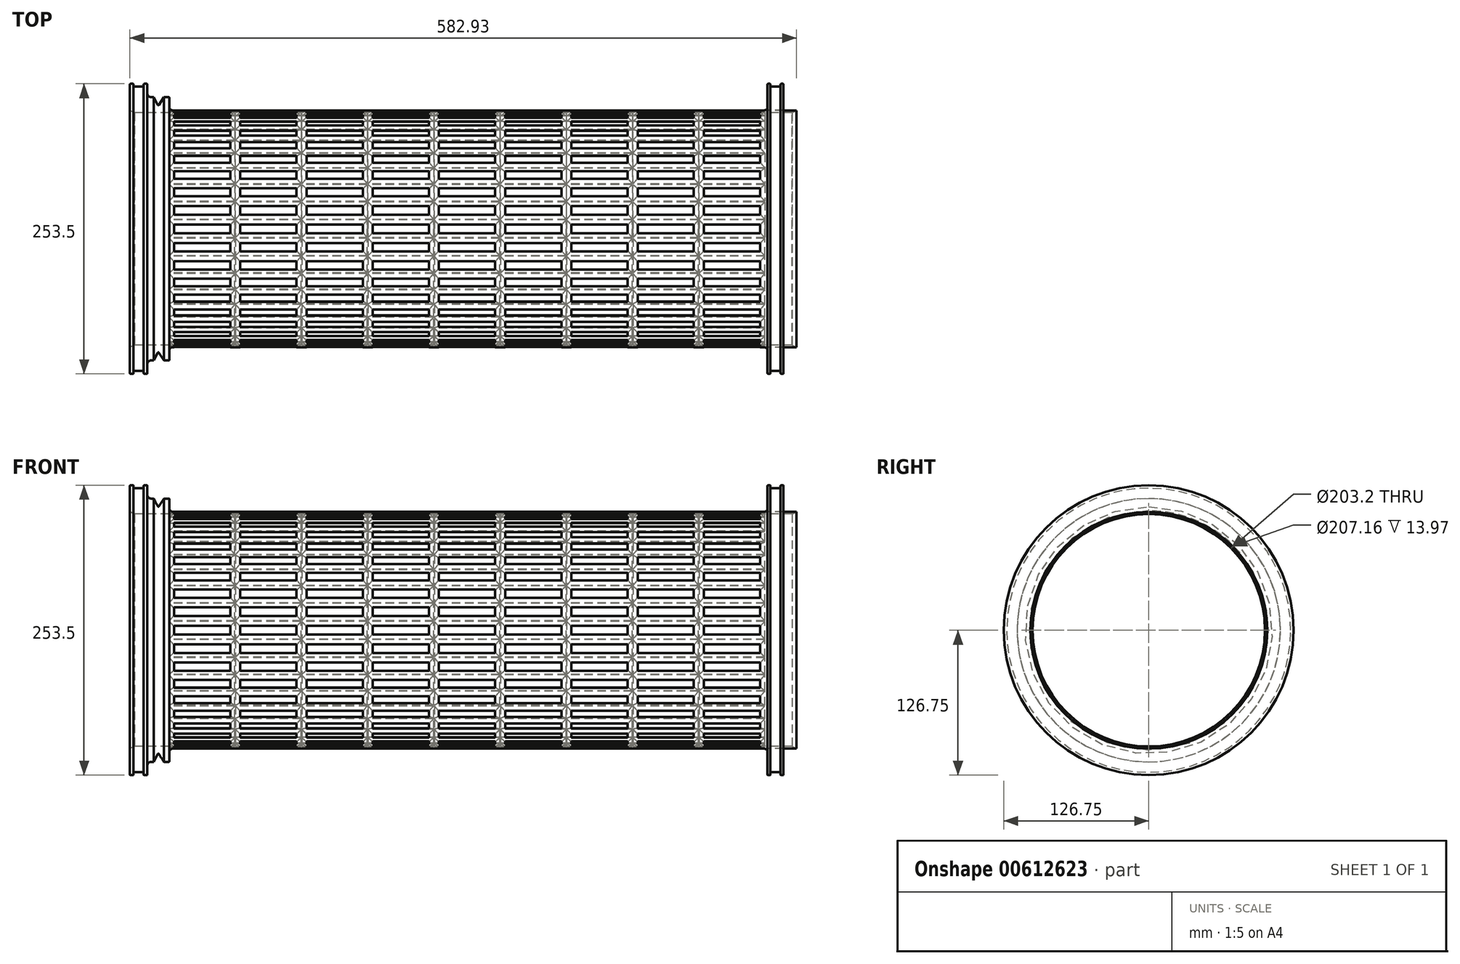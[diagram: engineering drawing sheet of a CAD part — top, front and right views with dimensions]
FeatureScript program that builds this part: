
annotation { "Feature Type Name" : "Feature", "Feature Type Description" : "" }
export const myFeature = defineFeature(function(context is Context, id is Id, definition is map)
    precondition{}
    {
        {
            var Q0;
            Q0=qCreatedBy(makeId("Top.planeOp"),FACE);
            var sketch = newSketch(context, id + "F0", { "sketchPlane" : qUnion([Q0])});
            skLineSegment(sketch, "E0", {"start": v(-334.6, 103.5) * mm, "end": v(-334.6, 126.75) * mm});
            skLineSegment(sketch, "E1", {"start": v(-334.6, 126.75) * mm, "end": v(-331.43, 126.75) * mm});
            skLineSegment(sketch, "E2", {"start": v(-319.37, 126.75) * mm, "end": v(-319.37, 103.5) * mm});
            skLineSegment(sketch, "E3", {"start": v(-319.37, 103.5) * mm, "end": v(219.75, 103.5) * mm});
            skLineSegment(sketch, "E4", {"start": v(222.92, 106.68) * mm, "end": v(222.92, 126.75) * mm});
            skLineSegment(sketch, "E5", {"start": v(236.9, 126.75) * mm, "end": v(236.9, 103.58) * mm});
            skLineSegment(sketch, "E6", {"start": v(236.9, 103.5) * mm, "end": v(248.32, 103.5) * mm});
            skLineSegment(sketch, "E7", {"start": v(-334.6, 101.6) * mm, "end": v(248.32, 101.6) * mm});
            skLineSegment(sketch, "E8", {"start": v(248.32, 101.6) * mm, "end": v(248.32, 103.5) * mm});
            skLineSegment(sketch, "E9", {"start": v(-331.43, 126.75) * mm, "end": v(-331.43, 124.2) * mm});
            skLineSegment(sketch, "E10", {"start": v(-322.54, 124.2) * mm, "end": v(-322.54, 126.75) * mm});
            skLineSegment(sketch, "E11.trimOffspring", {"start": v(-322.54, 126.75) * mm, "end": v(-319.37, 126.75) * mm});
            skLineSegment(sketch, "E12", {"start": v(225.46, 126.75) * mm, "end": v(225.46, 124.2) * mm});
            skLineSegment(sketch, "E13", {"start": v(-300.16, 103.5) * mm, "end": v(-300.16, 115.13) * mm});
            skPoint(sketch, "E13.endSnap0", {"position": v(-319.37, 115.13) * mm});
            skLineSegment(sketch, "E14", {"start": v(-300.16, 115.13) * mm, "end": v(-304.87, 115.13) * mm});
            skLineSegment(sketch, "E15", {"start": v(-313.74, 115.13) * mm, "end": v(-309.76, 107.51) * mm});
            skPoint(sketch, "E15.endSnap0", {"position": v(-309.76, 115.13) * mm});
            skLineSegment(sketch, "E16", {"start": v(-309.76, 107.51) * mm, "end": v(-304.87, 115.13) * mm});
            skLineSegment(sketch, "E17.trimOffspring", {"start": v(-313.74, 115.13) * mm, "end": v(-319.37, 115.13) * mm});
            skLineSegment(sketch, "E18", {"start": v(-334.6, 103.5) * mm, "end": v(-334.6, 101.6) * mm});
            skPoint(sketch, "E19.end.orphan", {"position": v(-353.66, 101.6) * mm});
            skLineSegment(sketch, "E20", {"start": v(222.92, 126.75) * mm, "end": v(225.46, 126.75) * mm});
            skPoint(sketch, "E20.startSnap0", {"position": v(225.46, 126.75) * mm});
            skPoint(sketch, "E21.start.orphan", {"position": v(222.92, 126.75) * mm});
            skPoint(sketch, "E22.orphan", {"position": v(225.46, 129.3) * mm});
            skPoint(sketch, "E23.trimOffspring.start.orphan", {"position": v(233.08, 126.75) * mm});
            skPoint(sketch, "E24.end.orphan", {"position": v(233.08, 124.2) * mm});
            skLineSegment(sketch, "E25", {"start": v(225.46, 124.2) * mm, "end": v(234.35, 124.2) * mm});
            skLineSegment(sketch, "E26", {"start": v(234.35, 124.2) * mm, "end": v(234.35, 126.11) * mm});
            skPoint(sketch, "E26.endSnap0", {"position": v(234.99, 126.11) * mm});
            skPoint(sketch, "E27.orphan", {"position": v(233.08, 125.48) * mm});
            skLineSegment(sketch, "E28", {"start": v(-331.43, 124.2) * mm, "end": v(-322.54, 124.2) * mm});
            skLineSegment(sketch, "E29", {"start": v(234.35, 126.11) * mm, "end": v(234.35, 126.75) * mm});
            skLineSegment(sketch, "E30", {"start": v(234.35, 126.75) * mm, "end": v(236.9, 126.75) * mm});
            skPoint(sketch, "E31.visualSharp", {"position": v(222.92, 103.5) * mm});
            skArc(sketch, "E31.filletArc", {"start": v(219.75, 103.5) * mm, "mid": v(222, 104.43) * mm, "end": v(222.92, 106.68) * mm});
            skLineSegment(sketch, "E32", {"start": v(236.9, 103.5) * mm, "end": v(222.92, 103.5) * mm});
            skLineSegment(sketch, "E33", {"start": v(222.92, 103.5) * mm, "end": v(222.92, 106.68) * mm});
            skLineSegment(sketch, "E34", {"start": v(236.9, 103.58) * mm, "end": v(222.92, 103.58) * mm});
            skSolve(sketch);
        }
        {
            var Q0;
            Q0=qCreatedBy(makeId("Top.planeOp"),FACE);
            var sketch = newSketch(context, id + "F1", { "sketchPlane" : qUnion([Q0])});
            skLineSegment(sketch, "E35", {"start": v(-76.35, 0) * mm, "end": v(75.96, 0) * mm});
            skSolve(sketch);
        }
        {
            var Q0;
            Q0=makeQuery(id+"F0.imprint","IMPRINT",FACE,{"disambiguationData":[TD([[makeQuery(id+"F0.imprint","IMPRINT",EDGE,{"derivedFrom":sQuery(id+"F0.wireOp",EDGE,"E0")}),-1.0]])]});
            var Q1;
            {var subQ0=sQuery(id+"F0.wireOp",EDGE,"E13");Q1=makeQuery(id+"F0.imprint","IMPRINT",FACE,{"disambiguationData":[TD([[makeQuery(id+"F0.imprint","IMPRINT",EDGE,{"derivedFrom":subQ0}),1.0]])]});}
            var Q2;
            Q2=qSketchRegion(id+"F3",true);
            var Q3;
            Q3=sQuery(id+"F1.wireOp",EDGE,"E35");
            revolve(context, id + "F2", {"entities" : qUnion([Q0, Q1, Q2]), "axis" : qUnion([Q3]), "revolveType" : RevolveType.FULL, "surfaceOperationType" : NewSurfaceOperationType.NEW});
        }
        {
            var Q0;
            Q0=qCreatedBy(makeId("Top.planeOp"),FACE);
            var sketch = newSketch(context, id + "F3", { "sketchPlane" : qUnion([Q0])});
            skPoint(sketch, "E36.middle", {"position": v(-205.28, 0) * mm});
            skPoint(sketch, "E37.middle", {"position": v(0, 0) * mm});
            skPoint(sketch, "E38.middle", {"position": v(166.22, 0) * mm});
            skLineSegment(sketch, "E39", {"start": v(-296.04, -3.81) * mm, "end": v(-296.04, 3.81) * mm});
            skPoint(sketch, "E40.orphan", {"position": v(-306.88, -3.81) * mm});
            skPoint(sketch, "E41.orphan", {"position": v(-306.88, 3.81) * mm});
            skPoint(sketch, "E38.left.start.orphan", {"position": v(229.72, -3.81) * mm});
            skPoint(sketch, "E42.orphan", {"position": v(229.72, 3.8) * mm});
            skLineSegment(sketch, "E43", {"start": v(-246.86, 3.81) * mm, "end": v(-246.86, -3.81) * mm});
            skLineSegment(sketch, "E44.trimOffspring", {"start": v(-246.86, 3.81) * mm, "end": v(-296.04, 3.81) * mm});
            skLineSegment(sketch, "E45.trimOffspring", {"start": v(-246.86, -3.81) * mm, "end": v(-296.04, -3.81) * mm});
            skPoint(sketch, "E46.end.orphan", {"position": v(-171.63, 3.81) * mm});
            skPoint(sketch, "E46.start.orphan", {"position": v(-171.63, -3.81) * mm});
            skPoint(sketch, "E47.end.orphan", {"position": v(-239.58, -3.81) * mm});
            skPoint(sketch, "E47.start.orphan", {"position": v(-239.58, 3.81) * mm});
            skPoint(sketch, "E36.left.end.orphan", {"position": v(-103.68, 3.81) * mm});
            skPoint(sketch, "E36.left.start.orphan", {"position": v(-103.68, -3.8) * mm});
            skPoint(sketch, "E37.bottom.end.orphan", {"position": v(-93.22, 3.98) * mm});
            skPoint(sketch, "E37.top.end.orphan", {"position": v(-93.22, -3.98) * mm});
            skPoint(sketch, "E37.left.end.orphan", {"position": v(93.22, -3.98) * mm});
            skPoint(sketch, "E37.left.start.orphan", {"position": v(93.22, 3.98) * mm});
            skPoint(sketch, "E38.bottom.end.orphan", {"position": v(102.72, -3.81) * mm});
            skPoint(sketch, "E38.top.end.orphan", {"position": v(102.72, 3.8) * mm});
            skLineSegment(sketch, "E48.1.0.0", {"start": v(-238.12, -3.81) * mm, "end": v(-238.12, 3.81) * mm});
            skLineSegment(sketch, "E48.1.0.1", {"start": v(-188.95, -3.81) * mm, "end": v(-238.12, -3.81) * mm});
            skLineSegment(sketch, "E48.1.0.2", {"start": v(-188.95, 3.81) * mm, "end": v(-188.95, -3.81) * mm});
            skLineSegment(sketch, "E48.1.0.3", {"start": v(-188.95, 3.81) * mm, "end": v(-238.12, 3.81) * mm});
            skLineSegment(sketch, "E48.2.0.0", {"start": v(-180.21, -3.81) * mm, "end": v(-180.21, 3.81) * mm});
            skLineSegment(sketch, "E48.2.0.1", {"start": v(-131.04, -3.81) * mm, "end": v(-180.21, -3.81) * mm});
            skLineSegment(sketch, "E48.2.0.2", {"start": v(-131.04, 3.81) * mm, "end": v(-131.04, -3.81) * mm});
            skLineSegment(sketch, "E48.2.0.3", {"start": v(-131.04, 3.81) * mm, "end": v(-180.21, 3.81) * mm});
            skLineSegment(sketch, "E48.3.0.0", {"start": v(-122.3, -3.81) * mm, "end": v(-122.3, 3.81) * mm});
            skLineSegment(sketch, "E48.3.0.1", {"start": v(-73.13, -3.81) * mm, "end": v(-122.3, -3.81) * mm});
            skLineSegment(sketch, "E48.3.0.2", {"start": v(-73.13, 3.81) * mm, "end": v(-73.13, -3.81) * mm});
            skLineSegment(sketch, "E48.3.0.3", {"start": v(-73.13, 3.81) * mm, "end": v(-122.3, 3.81) * mm});
            skLineSegment(sketch, "E48.4.0.0", {"start": v(-64.39, -3.81) * mm, "end": v(-64.39, 3.81) * mm});
            skLineSegment(sketch, "E48.4.0.1", {"start": v(-15.22, -3.81) * mm, "end": v(-64.39, -3.81) * mm});
            skLineSegment(sketch, "E48.4.0.2", {"start": v(-15.22, 3.81) * mm, "end": v(-15.22, -3.81) * mm});
            skLineSegment(sketch, "E48.4.0.3", {"start": v(-15.22, 3.81) * mm, "end": v(-64.39, 3.81) * mm});
            skLineSegment(sketch, "E48.5.0.0", {"start": v(-6.48, -3.81) * mm, "end": v(-6.48, 3.81) * mm});
            skLineSegment(sketch, "E48.5.0.1", {"start": v(42.7, -3.81) * mm, "end": v(-6.48, -3.81) * mm});
            skLineSegment(sketch, "E48.5.0.2", {"start": v(42.7, 3.81) * mm, "end": v(42.7, -3.81) * mm});
            skLineSegment(sketch, "E48.5.0.3", {"start": v(42.7, 3.81) * mm, "end": v(-6.48, 3.81) * mm});
            skLineSegment(sketch, "E48.6.0.0", {"start": v(51.44, -3.81) * mm, "end": v(51.44, 3.81) * mm});
            skLineSegment(sketch, "E48.6.0.1", {"start": v(100.6, -3.81) * mm, "end": v(51.44, -3.81) * mm});
            skLineSegment(sketch, "E48.6.0.2", {"start": v(100.6, 3.81) * mm, "end": v(100.6, -3.81) * mm});
            skLineSegment(sketch, "E48.6.0.3", {"start": v(100.6, 3.81) * mm, "end": v(51.44, 3.81) * mm});
            skLineSegment(sketch, "E48.7.0.0", {"start": v(109.35, -3.81) * mm, "end": v(109.35, 3.81) * mm});
            skLineSegment(sketch, "E48.7.0.1", {"start": v(158.52, -3.81) * mm, "end": v(109.35, -3.81) * mm});
            skLineSegment(sketch, "E48.7.0.2", {"start": v(158.52, 3.81) * mm, "end": v(158.52, -3.81) * mm});
            skLineSegment(sketch, "E48.7.0.3", {"start": v(158.52, 3.81) * mm, "end": v(109.35, 3.81) * mm});
            skLineSegment(sketch, "E48.8.0.0", {"start": v(167.26, -3.81) * mm, "end": v(167.26, 3.81) * mm});
            skLineSegment(sketch, "E48.8.0.1", {"start": v(216.43, -3.81) * mm, "end": v(167.26, -3.81) * mm});
            skLineSegment(sketch, "E48.8.0.2", {"start": v(216.43, 3.81) * mm, "end": v(216.43, -3.81) * mm});
            skLineSegment(sketch, "E48.8.0.3", {"start": v(216.43, 3.81) * mm, "end": v(167.26, 3.81) * mm});
            skLineSegment(sketch, "E48.direction1", {"start": v(-296.04, -3.81) * mm, "end": v(-238.12, -3.81) * mm, "construction": true});
            skSolve(sketch);
        }
        {
            var Q0;
            Q0=qSketchRegion(id+"F3",true);
            extrude(context, id + "F4", {"entities" : qUnion([Q0]), "depth" : 114.3 * mm, "offsetDistance" : 25.4 * mm});
        }
        {
            var Q0;
            Q0=makeQuery(id+"F4.opExtrude","SWEPT_BODY",BODY,{"disambiguationData":[OSD([sQuery(id+"F3.wireOp",EDGE,"E48.8.0.0"),sQuery(id+"F3.wireOp",EDGE,"E48.8.0.1"),sQuery(id+"F3.wireOp",EDGE,"E48.8.0.2"),sQuery(id+"F3.wireOp",EDGE,"E48.8.0.3")])]});
            var Q1;
            Q1=makeQuery(id+"F4.opExtrude","SWEPT_BODY",BODY,{"disambiguationData":[OSD([sQuery(id+"F3.wireOp",EDGE,"E48.7.0.0"),sQuery(id+"F3.wireOp",EDGE,"E48.7.0.1"),sQuery(id+"F3.wireOp",EDGE,"E48.7.0.2"),sQuery(id+"F3.wireOp",EDGE,"E48.7.0.3")])]});
            var Q2;
            Q2=makeQuery(id+"F4.opExtrude","SWEPT_BODY",BODY,{"disambiguationData":[OSD([sQuery(id+"F3.wireOp",EDGE,"E48.6.0.0"),sQuery(id+"F3.wireOp",EDGE,"E48.6.0.1"),sQuery(id+"F3.wireOp",EDGE,"E48.6.0.2"),sQuery(id+"F3.wireOp",EDGE,"E48.6.0.3")])]});
            var Q3;
            Q3=makeQuery(id+"F4.opExtrude","SWEPT_BODY",BODY,{"disambiguationData":[OSD([sQuery(id+"F3.wireOp",EDGE,"E48.5.0.0"),sQuery(id+"F3.wireOp",EDGE,"E48.5.0.1"),sQuery(id+"F3.wireOp",EDGE,"E48.5.0.2"),sQuery(id+"F3.wireOp",EDGE,"E48.5.0.3")])]});
            var Q4;
            Q4=makeQuery(id+"F4.opExtrude","SWEPT_BODY",BODY,{"disambiguationData":[OSD([sQuery(id+"F3.wireOp",EDGE,"E48.4.0.0"),sQuery(id+"F3.wireOp",EDGE,"E48.4.0.1"),sQuery(id+"F3.wireOp",EDGE,"E48.4.0.2"),sQuery(id+"F3.wireOp",EDGE,"E48.4.0.3")])]});
            var Q5;
            Q5=makeQuery(id+"F4.opExtrude","SWEPT_BODY",BODY,{"disambiguationData":[OSD([sQuery(id+"F3.wireOp",EDGE,"E48.3.0.0"),sQuery(id+"F3.wireOp",EDGE,"E48.3.0.1"),sQuery(id+"F3.wireOp",EDGE,"E48.3.0.2"),sQuery(id+"F3.wireOp",EDGE,"E48.3.0.3")])]});
            var Q6;
            Q6=makeQuery(id+"F4.opExtrude","SWEPT_BODY",BODY,{"disambiguationData":[OSD([sQuery(id+"F3.wireOp",EDGE,"E48.2.0.0"),sQuery(id+"F3.wireOp",EDGE,"E48.2.0.1"),sQuery(id+"F3.wireOp",EDGE,"E48.2.0.2"),sQuery(id+"F3.wireOp",EDGE,"E48.2.0.3")])]});
            var Q7;
            Q7=makeQuery(id+"F4.opExtrude","SWEPT_BODY",BODY,{"disambiguationData":[OSD([sQuery(id+"F3.wireOp",EDGE,"E48.1.0.0"),sQuery(id+"F3.wireOp",EDGE,"E48.1.0.1"),sQuery(id+"F3.wireOp",EDGE,"E48.1.0.2"),sQuery(id+"F3.wireOp",EDGE,"E48.1.0.3")])]});
            var Q8;
            Q8=makeQuery(id+"F4.opExtrude","SWEPT_BODY",BODY,{"disambiguationData":[OSD([sQuery(id+"F3.wireOp",EDGE,"E39"),sQuery(id+"F3.wireOp",EDGE,"E43"),sQuery(id+"F3.wireOp",EDGE,"E44.trimOffspring"),sQuery(id+"F3.wireOp",EDGE,"E45.trimOffspring")])]});
            var Q9;
            Q9=makeQuery(id+"F2.opRevolve","SWEPT_FACE",FACE,{"disambiguationData":[OSD([sQuery(id+"F0.wireOp",EDGE,"E7")])]});
            circularPattern(context, id + "F5", {"operationType" : NewBodyOperationType.REMOVE, "entities" : qUnion([Q0, Q1, Q2, Q3, Q4, Q5, Q6, Q7, Q8]), "axis" : qUnion([Q9]), "angle" : 360 * degree, "instanceCount" : 40, "equalSpace" : true});
        }
        {
            var Q0;
            Q0=makeQuery(id+"F2.opRevolve","SWEPT_FACE",FACE,{"disambiguationData":[OSD([sQuery(id+"F0.wireOp",EDGE,"E7")])]});
            chamfer(context, id + "F6", {"entities" : qUnion([Q0]), "chamferType" : ChamferType.TWO_OFFSETS, "width1" : 4.06 * mm, "oppositeDirection" : false, "width2" : 1.9 * mm});
        }
        {
            var Q0;
            Q0=makeQuery(id+"F2.opRevolve","SWEPT_EDGE",EDGE,{"disambiguationData":[OSD([sQuery(id+"F0.wireOp",EDGE,"E2"),sQuery(id+"F0.wireOp",EDGE,"E17.trimOffspring")])]});
            var Q1;
            Q1=makeQuery(id+"F2.opRevolve","SWEPT_EDGE",EDGE,{"disambiguationData":[OSD([sQuery(id+"F0.wireOp",EDGE,"E3"),sQuery(id+"F0.wireOp",EDGE,"E13")])]});
            var Q2;
            Q2=makeQuery(id+"F2.opRevolve","SWEPT_EDGE",EDGE,{"disambiguationData":[OSD([sQuery(id+"F0.wireOp",EDGE,"E3"),sQuery(id+"F0.wireOp",EDGE,"E4")])]});
            var Q3;
            Q3=makeQuery(id+"F2.opRevolve","SWEPT_EDGE",EDGE,{"disambiguationData":[OSD([sQuery(id+"F0.wireOp",EDGE,"E5"),sQuery(id+"F0.wireOp",EDGE,"E6")])]});
            fillet(context, id + "F7", {"entities" : qUnion([Q0, Q1, Q2, Q3]), "radius" : 3.17 * mm, "tangentPropagation" : true, "allowEdgeOverflow" : false});
        }
        {
            var Q0;
            Q0=makeQuery(id+"F2.opRevolve","SWEPT_EDGE",EDGE,{"disambiguationData":[OSD([sQuery(id+"F0.wireOp",EDGE,"E10"),sQuery(id+"F0.wireOp",EDGE,"E28")])]});
            var Q1;
            Q1=makeQuery(id+"F2.opRevolve","SWEPT_EDGE",EDGE,{"disambiguationData":[OSD([sQuery(id+"F0.wireOp",EDGE,"E15"),sQuery(id+"F0.wireOp",EDGE,"E16")])]});
            var Q2;
            Q2=makeQuery(id+"F2.opRevolve","SWEPT_EDGE",EDGE,{"disambiguationData":[OSD([sQuery(id+"F0.wireOp",EDGE,"E13"),sQuery(id+"F0.wireOp",EDGE,"E14")])]});
            var Q3;
            Q3=makeQuery(id+"F2.opRevolve","SWEPT_EDGE",EDGE,{"disambiguationData":[OSD([sQuery(id+"F0.wireOp",EDGE,"E25"),sQuery(id+"F0.wireOp",EDGE,"E26")])]});
            var Q4;
            Q4=makeQuery(id+"F2.opRevolve","SWEPT_EDGE",EDGE,{"disambiguationData":[OSD([sQuery(id+"F0.wireOp",EDGE,"E4"),sQuery(id+"F0.wireOp",EDGE,"E20")])]});
            var Q5;
            Q5=makeQuery(id+"F2.opRevolve","SWEPT_EDGE",EDGE,{"disambiguationData":[OSD([sQuery(id+"F0.wireOp",EDGE,"E29"),sQuery(id+"F0.wireOp",EDGE,"E30")])]});
            var Q6;
            Q6=makeQuery(id+"F2.opRevolve","SWEPT_EDGE",EDGE,{"disambiguationData":[OSD([sQuery(id+"F0.wireOp",EDGE,"E5"),sQuery(id+"F0.wireOp",EDGE,"E30")])]});
            var Q7;
            Q7=makeQuery(id+"F2.opRevolve","SWEPT_EDGE",EDGE,{"disambiguationData":[OSD([sQuery(id+"F0.wireOp",EDGE,"E12"),sQuery(id+"F0.wireOp",EDGE,"E20")])]});
            var Q8;
            Q8=makeQuery(id+"F2.opRevolve","SWEPT_EDGE",EDGE,{"disambiguationData":[OSD([sQuery(id+"F0.wireOp",EDGE,"E10"),sQuery(id+"F0.wireOp",EDGE,"E11.trimOffspring")])]});
            var Q9;
            Q9=makeQuery(id+"F2.opRevolve","SWEPT_EDGE",EDGE,{"disambiguationData":[OSD([sQuery(id+"F0.wireOp",EDGE,"E0"),sQuery(id+"F0.wireOp",EDGE,"E1")])]});
            var Q10;
            Q10=makeQuery(id+"F2.opRevolve","SWEPT_EDGE",EDGE,{"disambiguationData":[OSD([sQuery(id+"F0.wireOp",EDGE,"E1"),sQuery(id+"F0.wireOp",EDGE,"E9")])]});
            var Q11;
            Q11=makeQuery(id+"F2.opRevolve","SWEPT_EDGE",EDGE,{"disambiguationData":[OSD([sQuery(id+"F0.wireOp",EDGE,"E2"),sQuery(id+"F0.wireOp",EDGE,"E11.trimOffspring")])]});
            fillet(context, id + "F8", {"entities" : qUnion([Q0, Q1, Q2, Q3, Q4, Q5, Q6, Q7, Q8, Q9, Q10, Q11]), "radius" : 0.5 * mm, "tangentPropagation" : true, "allowEdgeOverflow" : false});
        }
        {
            var Q0;
            Q0=makeQuery(id+"F0.imprint","IMPRINT",FACE,{"disambiguationData":[TD([[makeQuery(id+"F0.imprint","IMPRINT",EDGE,{"derivedFrom":sQuery(id+"F0.wireOp",EDGE,"E4")}),-1.0]])]});
            var Q1;
            Q1=sQuery(id+"F1.wireOp",EDGE,"E35");
            revolve(context, id + "F9", {"surfaceOperationType" : NewSurfaceOperationType.NEW, "entities" : qUnion([Q0]), "axis" : qUnion([Q1]), "revolveType" : RevolveType.FULL});
        }
        {
            var Q0;
            Q0=makeQuery(id+"F9.opRevolve","SWEPT_EDGE",EDGE,{"disambiguationData":[OSD([sQuery(id+"F0.wireOp",EDGE,"E4"),sQuery(id+"F0.wireOp",EDGE,"E20")])]});
            var Q1;
            Q1=makeQuery(id+"F9.opRevolve","SWEPT_EDGE",EDGE,{"disambiguationData":[OSD([sQuery(id+"F0.wireOp",EDGE,"E12"),sQuery(id+"F0.wireOp",EDGE,"E20")])]});
            var Q2;
            Q2=makeQuery(id+"F9.opRevolve","SWEPT_EDGE",EDGE,{"disambiguationData":[OSD([sQuery(id+"F0.wireOp",EDGE,"E5"),sQuery(id+"F0.wireOp",EDGE,"E30")])]});
            var Q3;
            Q3=makeQuery(id+"F9.opRevolve","SWEPT_EDGE",EDGE,{"disambiguationData":[OSD([sQuery(id+"F0.wireOp",EDGE,"E29"),sQuery(id+"F0.wireOp",EDGE,"E30")])]});
            var Q4;
            Q4=makeQuery(id+"F9.opRevolve","SWEPT_EDGE",EDGE,{"disambiguationData":[OSD([sQuery(id+"F0.wireOp",EDGE,"E25"),sQuery(id+"F0.wireOp",EDGE,"E26")])]});
            fillet(context, id + "F10", {"entities" : qUnion([Q0, Q1, Q2, Q3, Q4]), "radius" : 0.5 * mm, "tangentPropagation" : true, "allowEdgeOverflow" : false});
        }
    });
